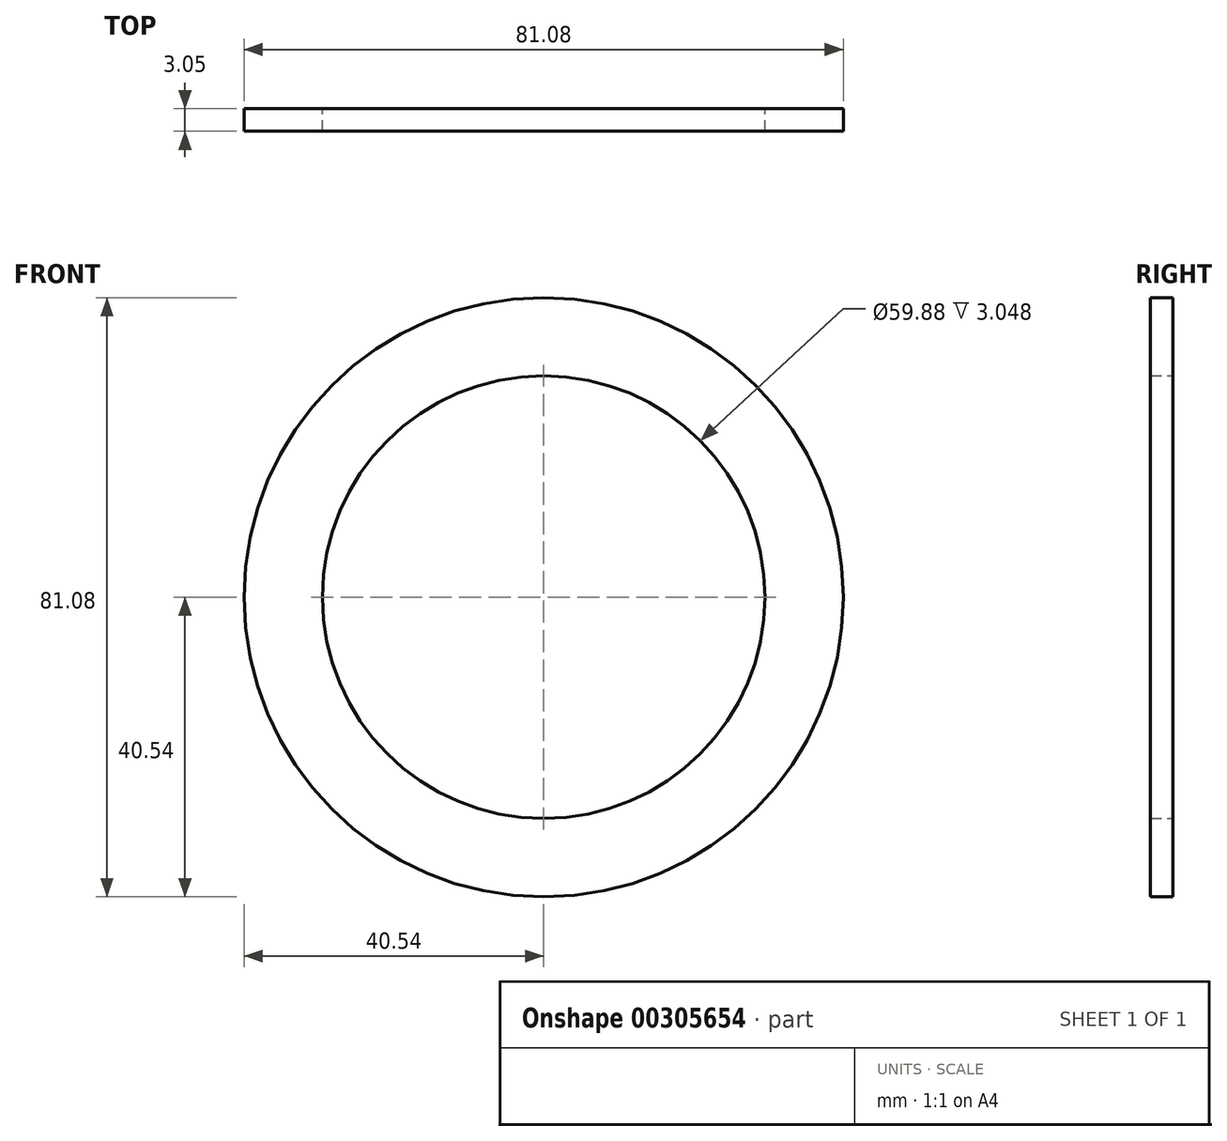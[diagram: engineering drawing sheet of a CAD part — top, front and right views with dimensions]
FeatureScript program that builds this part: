
annotation { "Feature Type Name" : "Feature", "Feature Type Description" : "" }
export const myFeature = defineFeature(function(context is Context, id is Id, definition is map)
    precondition{}
    {
        {
            var Q0;
            Q0=qCreatedBy(makeId("Front.planeOp"),FACE);
            var sketch = newSketch(context, id + "F0", { "sketchPlane" : qUnion([Q0])});
            skCircle(sketch, "E0", {"center": v(0, 0) * mm, "radius": 40.54 * mm});
            skCircle(sketch, "E1", {"center": v(0, 0) * mm, "radius": 29.94 * mm});
            skCircle(sketch, "E2", {"center": v(0, 0) * mm, "radius": 27.97 * mm});
            skSolve(sketch);
        }
        {
            var Q0;
            Q0=makeQuery(id+"F0.imprint","IMPRINT",FACE,{"disambiguationData":[TD([[makeQuery(id+"F0.imprint","IMPRINT",EDGE,{"derivedFrom":sQuery(id+"F0.wireOp",EDGE,"E0")}),1.0]])]});
            var Q1;
            Q1=sQuery(id+"F0.wireOp",EDGE,"E1");
            var Q2;
            Q2=sQuery(id+"F0.wireOp",EDGE,"E2");
            var Q3;
            Q3=sQuery(id+"F0.wireOp",EDGE,"E0");
            extrude(context, id + "F1", {"entities" : qUnion([Q0]), "surfaceEntities" : qUnion([Q1, Q2, Q3]), "depth" : 3.05 * mm});
        }
    });
